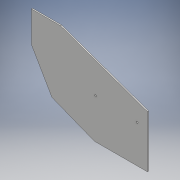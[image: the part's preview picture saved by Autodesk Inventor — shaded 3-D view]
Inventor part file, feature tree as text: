
AUTODESK INVENTOR PART (.ipt)
format: ipt  version: 2018.3 (Build 223284000, 284)  size: 113,664 bytes
history: native  units: mm
features: extrude x2, sketch x2, projected_geometry x1
ambient origin geometry x8: Origin, YZ Plane, XZ Plane, XY Plane, X Axis, Y Axis, Z Axis, Center Point
bodies: Body1 (feature_tree)
feature tree (5):
  extrude  "押し出し1"  Depth=6.0mm TaperAngle=0.0deg
  extrude  "押し出し2"  Depth=9.0mm
  sketch  "スケッチ3"
  projected_geometry  "投影ループ2"
  sketch  "スケッチ4"
